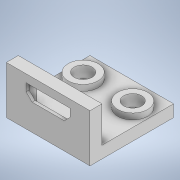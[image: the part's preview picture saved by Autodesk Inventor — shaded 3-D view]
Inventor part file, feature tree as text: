
AUTODESK INVENTOR PART (.ipt)
format: ipt  version: 2022 (Build 260153000, 153)  size: 169,984 bytes
history: native  units: mm
features: extrude x6, sketch x6
ambient origin geometry x8: Origin, YZ Plane, XZ Plane, XY Plane, X Axis, Y Axis, Z Axis, Center Point
bodies: Solid1 (feature_tree)
feature tree (12):
  extrude  "Extrusion1"  Depth=14.0mm
  extrude  "Extrusion2"  Depth=2.0mm
  extrude  "Extrusion3"  Depth=5.0mm
  extrude  "Extrusion4"  Depth=10.0mm
  extrude  "Extrusion5"  Depth=10.0mm
  extrude  "Extrusion6"  Depth=1.0mm TaperAngle=0.0deg
  sketch  "Sketch1"  dims[d0=14.0mm d1=14.0mm]
  sketch  "Sketch2"  dims[d2=2.0mm d3=0.0mm d4=2.0mm]
  sketch  "Sketch3"  dims[d5=6.0mm d6=0.0mm d7=5.0mm]
  sketch  "Sketch4"  dims[d8=5.0mm d9=10.0mm]
  sketch  "Sketch5"  dims[d10=10.0mm d11=8.3mm]
  sketch  "Sketch6"  dims[d13=0.35mm d14=1.0mm d15=0.0mm d16=3.0mm d17=3.0mm d18=2.0mm d19=0.0mm d20=1.4mm d21=7.4mm d22=2.3mm d27=3.3mm d28=135.0deg d29=1.0mm d30=1.0mm d31=2.0mm d32=0.0mm d33=0.2mm d34=0.2mm d35=0.2mm d36=1.5mm d37=0.0mm]
